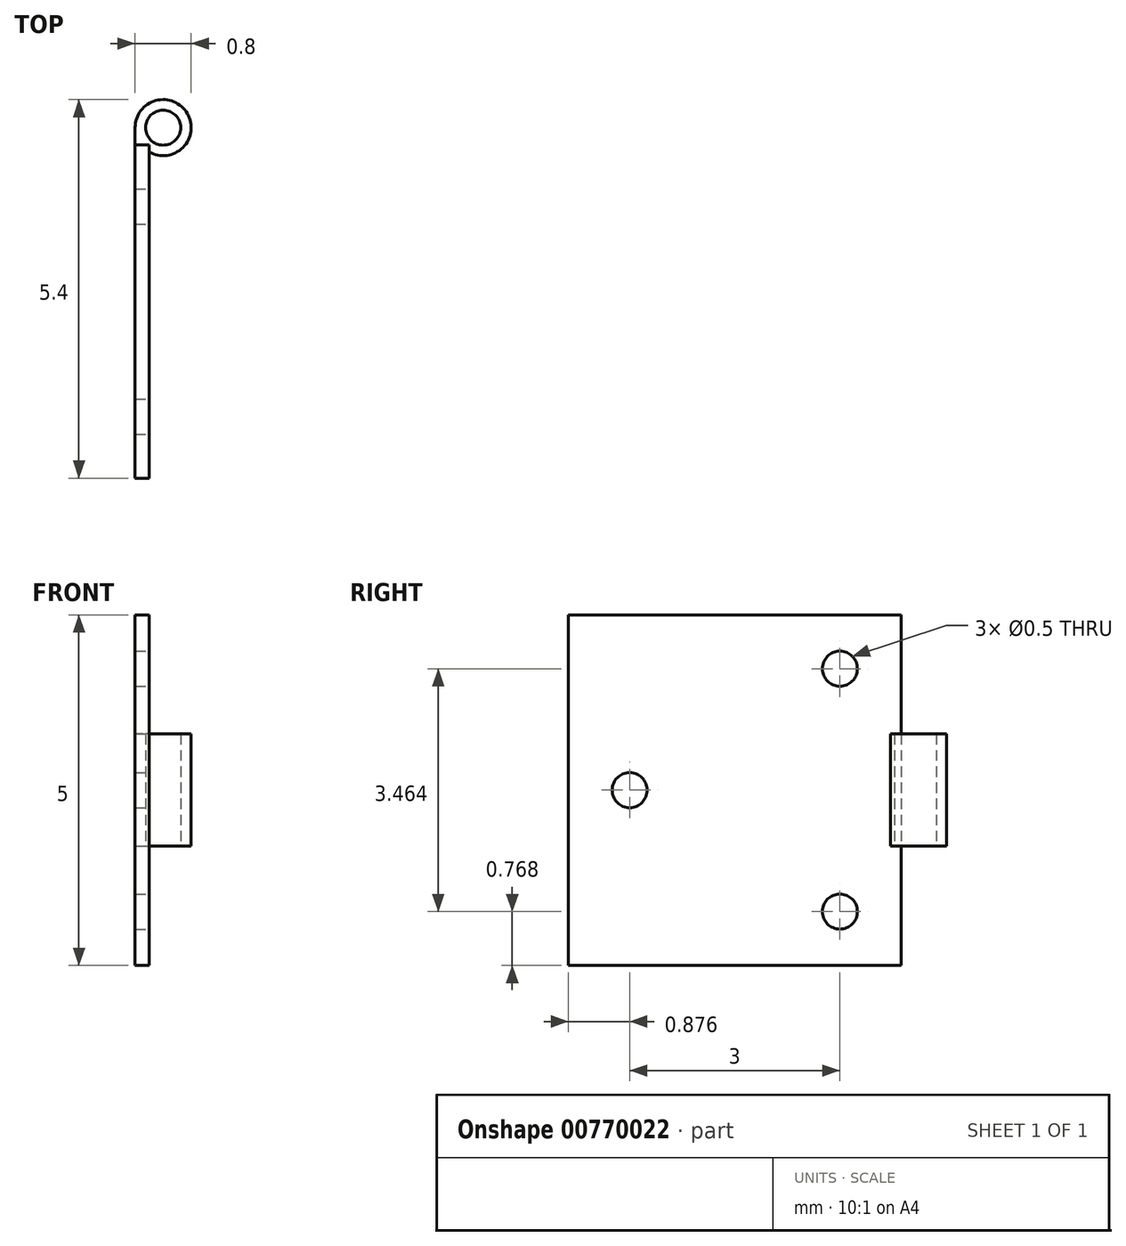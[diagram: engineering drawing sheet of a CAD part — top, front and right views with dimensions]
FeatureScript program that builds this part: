
annotation { "Feature Type Name" : "Feature", "Feature Type Description" : "" }
export const myFeature = defineFeature(function(context is Context, id is Id, definition is map)
    precondition{}
    {
        {
            var Q0;
            Q0=qCreatedBy(makeId("Front.planeOp"),FACE);
            var sketch = newSketch(context, id + "F0", { "sketchPlane" : qUnion([Q0])});
            skLineSegment(sketch, "E0.bottom", {"start": v(-0.1, 2.5) * mm, "end": v(0.1, 2.5) * mm});
            skLineSegment(sketch, "E0.top", {"start": v(-0.1, -2.5) * mm, "end": v(0.1, -2.5) * mm});
            skLineSegment(sketch, "E0.left", {"start": v(-0.1, 2.5) * mm, "end": v(-0.1, -2.5) * mm});
            skLineSegment(sketch, "E0.right", {"start": v(0.1, 2.5) * mm, "end": v(0.1, -2.5) * mm});
            skPoint(sketch, "E0.middle", {"position": v(0, 0) * mm});
            skSolve(sketch);
        }
        {
            var Q0;
            Q0 = qSketchRegion(id + "F0", true);
            extrude(context, id + "F1", {"entities" : qUnion([Q0]), "oppositeDirection" : true, "depth" : 5 * mm, "offsetDistance" : 25 * mm});
        }
        {
            var Q0;
            Q0=makeQuery(id+"F1.opExtrude","SWEPT_FACE",FACE,{"disambiguationData":[OSD([sQuery(id+"F0.wireOp",EDGE,"E0.top")])]});
            var sketch = newSketch(context, id + "F2", { "sketchPlane" : qUnion([Q0])});
            skCircle(sketch, "E1", {"center": v(0.3, -5) * mm, "radius": 0.4 * mm});
            skSolve(sketch);
        }
        {
            var Q0;
            Q0 = qSketchRegion(id + "F2", true);
            extrude(context, id + "F3", {"entities" : qUnion([Q0]), "operationType" : NewBodyOperationType.ADD, "oppositeDirection" : true, "depth" : 5 * mm, "offsetDistance" : 25 * mm});
        }
        {
            var Q0;
            Q0=makeQuery(id+"F3.boolean.opBoolean","MERGE",FACE,{"derivedFrom":[makeQuery(id+"F1.opExtrude","SWEPT_FACE",FACE,{"disambiguationData":[OSD([sQuery(id+"F0.wireOp",EDGE,"E0.top")])]}),makeQuery(id+"F3.opExtrude","CAP_FACE",FACE,{"disambiguationData":[OSD([sQuery(id+"F2.wireOp",EDGE,"E1")])],"isStart":true})]});
            var sketch = newSketch(context, id + "F4", { "sketchPlane" : qUnion([Q0])});
            skCircle(sketch, "E2", {"center": v(0.3, -5) * mm, "radius": 0.25 * mm});
            skSolve(sketch);
        }
        {
            var Q0;
            Q0 = qSketchRegion(id + "F4", true);
            extrude(context, id + "F5", {"entities" : qUnion([Q0]), "operationType" : NewBodyOperationType.REMOVE, "endBound" : BoundingType.THROUGH_ALL, "oppositeDirection" : true, "depth" : 25 * mm, "offsetDistance" : 25 * mm});
        }
        {
            var Q0;
            Q0=makeQuery(id+"F1.opExtrude","CAP_FACE",FACE,{"disambiguationData":[OSD([sQuery(id+"F0.wireOp",EDGE,"E0.bottom"),sQuery(id+"F0.wireOp",EDGE,"E0.top"),sQuery(id+"F0.wireOp",EDGE,"E0.left"),sQuery(id+"F0.wireOp",EDGE,"E0.right")])],"isStart":true});
            var sketch = newSketch(context, id + "F6", { "sketchPlane" : qUnion([Q0])});
            skLineSegment(sketch, "E3", {"start": v(0.1, 0) * mm, "end": v(0.94, 0) * mm});
            skLineSegment(sketch, "E4", {"start": v(0.94, 0) * mm, "end": v(0.94, 0.8) * mm});
            skLineSegment(sketch, "E5", {"start": v(0.94, 0) * mm, "end": v(0.94, -0.8) * mm});
            skLineSegment(sketch, "E6", {"start": v(0.94, 0.8) * mm, "end": v(0.1, 0.8) * mm});
            skLineSegment(sketch, "E7", {"start": v(0.1, 0.8) * mm, "end": v(0.1, -0.8) * mm});
            skLineSegment(sketch, "E8", {"start": v(0.1, -0.8) * mm, "end": v(0.94, -0.8) * mm});
            skLineSegment(sketch, "E9", {"start": v(0.1, 0.8) * mm, "end": v(0.1, 2.5) * mm});
            skLineSegment(sketch, "E10", {"start": v(0.1, 2.5) * mm, "end": v(0.94, 2.5) * mm});
            skLineSegment(sketch, "E11", {"start": v(0.94, 2.5) * mm, "end": v(0.94, 0.8) * mm});
            skLineSegment(sketch, "E12", {"start": v(0.1, -0.8) * mm, "end": v(0.1, -2.5) * mm});
            skLineSegment(sketch, "E13", {"start": v(0.1, -2.5) * mm, "end": v(0.94, -2.5) * mm});
            skLineSegment(sketch, "E14", {"start": v(0.94, -2.5) * mm, "end": v(0.94, -0.8) * mm});
            skSolve(sketch);
        }
        {
            var Q0;
            Q0=makeQuery(id+"F6.imprint","IMPRINT",FACE,{"disambiguationData":[TD([[makeQuery(id+"F6.imprint","IMPRINT",EDGE,{"derivedFrom":sQuery(id+"F6.wireOp",EDGE,"E6")}),-1.0]])]});
            var Q1;
            Q1=makeQuery(id+"F6.imprint","IMPRINT",FACE,{"disambiguationData":[TD([[makeQuery(id+"F6.imprint","IMPRINT",EDGE,{"derivedFrom":sQuery(id+"F6.wireOp",EDGE,"E8")}),-1.0]])]});
            extrude(context, id + "F7", {"entities" : qUnion([Q0, Q1]), "operationType" : NewBodyOperationType.REMOVE, "endBound" : BoundingType.THROUGH_ALL, "oppositeDirection" : true, "depth" : 25 * mm, "offsetDistance" : 25 * mm});
        }
        {
            var Q0;
            Q0=makeQuery(id+"F7.boolean.opBoolean","MERGE",FACE,{"derivedFrom":[makeQuery(id+"F1.opExtrude","SWEPT_FACE",FACE,{"disambiguationData":[OSD([sQuery(id+"F0.wireOp",EDGE,"E0.right")])]}),makeQuery(id+"F7.opExtrude","SWEPT_FACE",FACE,{"disambiguationData":[OSD([sQuery(id+"F6.wireOp",EDGE,"E9")])]}),makeQuery(id+"F7.opExtrude","SWEPT_FACE",FACE,{"disambiguationData":[OSD([sQuery(id+"F6.wireOp",EDGE,"E12")])]})]});
            var sketch = newSketch(context, id + "F8", { "sketchPlane" : qUnion([Q0])});
            skLineSegment(sketch, "E15", {"start": v(4.75, 0.8) * mm, "end": v(4.75, 2.5) * mm});
            skLineSegment(sketch, "E16", {"start": v(4.75, 2.5) * mm, "end": v(5.55, 2.5) * mm});
            skLineSegment(sketch, "E17", {"start": v(5.55, 2.5) * mm, "end": v(5.55, 0.8) * mm});
            skLineSegment(sketch, "E18", {"start": v(5.55, 0.8) * mm, "end": v(4.75, 0.8) * mm});
            skLineSegment(sketch, "E19", {"start": v(4.75, -0.8) * mm, "end": v(5.55, -0.8) * mm});
            skLineSegment(sketch, "E20", {"start": v(4.75, -0.8) * mm, "end": v(4.75, -2.5) * mm});
            skLineSegment(sketch, "E21", {"start": v(4.75, -2.5) * mm, "end": v(5.55, -2.5) * mm});
            skLineSegment(sketch, "E22", {"start": v(5.55, -2.5) * mm, "end": v(5.55, -0.8) * mm});
            skSolve(sketch);
        }
        {
            var Q0;
            Q0 = qSketchRegion(id + "F8", true);
            extrude(context, id + "F9", {"entities" : qUnion([Q0]), "operationType" : NewBodyOperationType.REMOVE, "endBound" : BoundingType.THROUGH_ALL, "oppositeDirection" : true, "depth" : 25 * mm, "offsetDistance" : 25 * mm});
        }
        {
            var Q0;
            Q0=makeQuery(id+"F7.boolean.opBoolean","MERGE",FACE,{"derivedFrom":[makeQuery(id+"F1.opExtrude","SWEPT_FACE",FACE,{"disambiguationData":[OSD([sQuery(id+"F0.wireOp",EDGE,"E0.right")])]}),makeQuery(id+"F7.opExtrude","SWEPT_FACE",FACE,{"disambiguationData":[OSD([sQuery(id+"F6.wireOp",EDGE,"E9")])]}),makeQuery(id+"F7.opExtrude","SWEPT_FACE",FACE,{"disambiguationData":[OSD([sQuery(id+"F6.wireOp",EDGE,"E12")])]})]});
            var sketch = newSketch(context, id + "F10", { "sketchPlane" : qUnion([Q0])});
            skPoint(sketch, "E23.cCircle.centerSnap0", {"position": v(2.38, -2.5) * mm});
            skLineSegment(sketch, "E24", {"start": v(2.38, 0) * mm, "end": v(2.88, 0) * mm});
            skCircle(sketch, "E25.cCircle", {"center": v(2.88, 0) * mm, "radius": 1 * mm, "construction": true});
            skLineSegment(sketch, "E25.0", {"start": v(3.88, 1.73) * mm, "end": v(3.88, -1.73) * mm});
            skLineSegment(sketch, "E25.1", {"start": v(3.88, -1.73) * mm, "end": v(0.88, 0) * mm});
            skLineSegment(sketch, "E25.2", {"start": v(0.88, 0) * mm, "end": v(3.88, 1.73) * mm});
            skPoint(sketch, "E25.0.midPoint", {"position": v(3.88, 0) * mm});
            skCircle(sketch, "E26", {"center": v(3.88, 1.73) * mm, "radius": 0.25 * mm});
            skCircle(sketch, "E27", {"center": v(3.88, -1.73) * mm, "radius": 0.25 * mm});
            skCircle(sketch, "E28", {"center": v(0.88, 0) * mm, "radius": 0.25 * mm});
            skSolve(sketch);
        }
        {
            var Q0;
            {var subQ0=sQuery(id+"F10.wireOp",EDGE,"E25.2");var subQ1=sQuery(id+"F10.wireOp",EDGE,"E25.0");var subQ2=makeQuery(id+"F10.imprint","INTERSECT",VERTEX,{"derivedFrom":[subQ1,subQ0]});Q0=makeQuery(id+"F10.imprint","IMPRINT",FACE,{"disambiguationData":[TD([[makeQuery(id+"F10.imprint","IMPRINT",EDGE,{"disambiguationData":[TD([[subQ2,-1.0]])],"derivedFrom":subQ1}),-1.0]])]});}
            var Q1;
            {var subQ0=sQuery(id+"F10.wireOp",EDGE,"E25.2");var subQ1=sQuery(id+"F10.wireOp",EDGE,"E25.0");var subQ2=makeQuery(id+"F10.imprint","INTERSECT",VERTEX,{"derivedFrom":[subQ1,subQ0]});Q1=makeQuery(id+"F10.imprint","IMPRINT",FACE,{"disambiguationData":[TD([[makeQuery(id+"F10.imprint","IMPRINT",EDGE,{"disambiguationData":[TD([[subQ2,-1.0]])],"derivedFrom":subQ1}),1.0]])]});}
            var Q2;
            {var subQ0=sQuery(id+"F10.wireOp",EDGE,"E25.1");var subQ1=sQuery(id+"F10.wireOp",EDGE,"E25.0");var subQ2=makeQuery(id+"F10.imprint","INTERSECT",VERTEX,{"derivedFrom":[subQ1,subQ0]});Q2=makeQuery(id+"F10.imprint","IMPRINT",FACE,{"disambiguationData":[TD([[makeQuery(id+"F10.imprint","IMPRINT",EDGE,{"disambiguationData":[TD([[subQ2,1.0]])],"derivedFrom":subQ1}),-1.0]])]});}
            var Q3;
            {var subQ0=sQuery(id+"F10.wireOp",EDGE,"E25.1");var subQ1=sQuery(id+"F10.wireOp",EDGE,"E25.0");var subQ2=makeQuery(id+"F10.imprint","INTERSECT",VERTEX,{"derivedFrom":[subQ1,subQ0]});Q3=makeQuery(id+"F10.imprint","IMPRINT",FACE,{"disambiguationData":[TD([[makeQuery(id+"F10.imprint","IMPRINT",EDGE,{"disambiguationData":[TD([[subQ2,1.0]])],"derivedFrom":subQ1}),1.0]])]});}
            var Q4;
            {var subQ0=sQuery(id+"F10.wireOp",EDGE,"E25.2");var subQ1=sQuery(id+"F10.wireOp",EDGE,"E25.1");var subQ2=makeQuery(id+"F10.imprint","INTERSECT",VERTEX,{"derivedFrom":[subQ1,subQ0]});Q4=makeQuery(id+"F10.imprint","IMPRINT",FACE,{"disambiguationData":[TD([[makeQuery(id+"F10.imprint","IMPRINT",EDGE,{"disambiguationData":[TD([[subQ2,1.0]])],"derivedFrom":subQ1}),1.0]])]});}
            var Q5;
            {var subQ0=sQuery(id+"F10.wireOp",EDGE,"E25.2");var subQ1=sQuery(id+"F10.wireOp",EDGE,"E25.1");var subQ2=makeQuery(id+"F10.imprint","INTERSECT",VERTEX,{"derivedFrom":[subQ1,subQ0]});Q5=makeQuery(id+"F10.imprint","IMPRINT",FACE,{"disambiguationData":[TD([[makeQuery(id+"F10.imprint","IMPRINT",EDGE,{"disambiguationData":[TD([[subQ2,1.0]])],"derivedFrom":subQ1}),-1.0]])]});}
            extrude(context, id + "F11", {"entities" : qUnion([Q0, Q1, Q2, Q3, Q4, Q5]), "operationType" : NewBodyOperationType.REMOVE, "endBound" : BoundingType.THROUGH_ALL, "oppositeDirection" : true, "depth" : 25 * mm, "offsetDistance" : 25 * mm});
        }
    });
